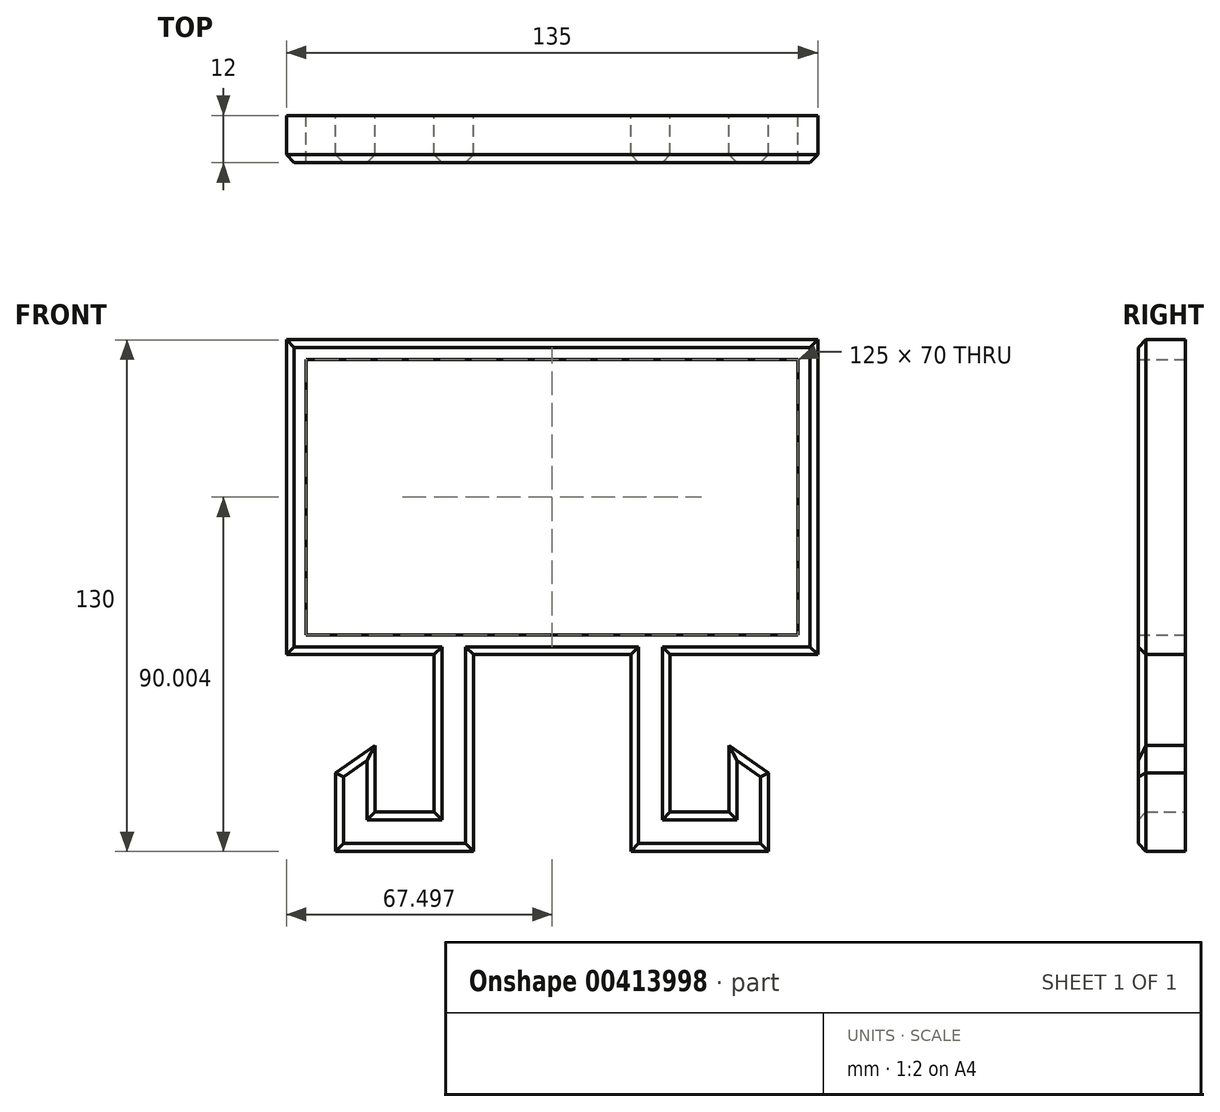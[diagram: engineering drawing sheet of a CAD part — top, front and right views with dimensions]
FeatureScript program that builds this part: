
annotation { "Feature Type Name" : "Feature", "Feature Type Description" : "" }
export const myFeature = defineFeature(function(context is Context, id is Id, definition is map)
    precondition{}
    {
        {
            var Q0;
            Q0=qCreatedBy(makeId("Front.planeOp"),FACE);
            var sketch = newSketch(context, id + "F0", { "sketchPlane" : qUnion([Q0])});
            skLineSegment(sketch, "E0.bottom", {"start": v(-108.38, 64.35) * mm, "end": v(16.62, 64.35) * mm});
            skLineSegment(sketch, "E0.top", {"start": v(-108.38, -5.65) * mm, "end": v(16.62, -5.65) * mm});
            skLineSegment(sketch, "E0.left", {"start": v(-108.38, 64.35) * mm, "end": v(-108.38, -5.65) * mm});
            skLineSegment(sketch, "E0.right", {"start": v(16.62, 64.35) * mm, "end": v(16.62, -5.65) * mm});
            skLineSegment(sketch, "E1.0", {"start": v(-113.38, 69.35) * mm, "end": v(21.62, 69.35) * mm});
            skLineSegment(sketch, "E1.1", {"start": v(-113.38, 69.35) * mm, "end": v(-113.38, -10.65) * mm});
            skLineSegment(sketch, "E1.2", {"start": v(-113.38, -10.65) * mm, "end": v(21.62, -10.65) * mm});
            skLineSegment(sketch, "E1.3", {"start": v(21.62, 69.35) * mm, "end": v(21.62, -10.65) * mm});
            skPoint(sketch, "E2", {"position": v(-73.94, -5.65) * mm});
            skPoint(sketch, "E3", {"position": v(-45.88, -10.65) * mm});
            skLineSegment(sketch, "E4", {"start": v(-45.88, -10.65) * mm, "end": v(-45.88, 23.81) * mm, "construction": true});
            skPoint(sketch, "E5", {"position": v(-65.88, -10.65) * mm});
            skLineSegment(sketch, "E6", {"start": v(-65.88, -10.65) * mm, "end": v(-65.88, -60.65) * mm});
            skLineSegment(sketch, "E7", {"start": v(-65.88, -60.65) * mm, "end": v(-100.88, -60.65) * mm});
            skLineSegment(sketch, "E8", {"start": v(-75.88, -50.65) * mm, "end": v(-75.88, -10.65) * mm});
            skLineSegment(sketch, "E9", {"start": v(-90.88, -40.65) * mm, "end": v(-90.88, -50.65) * mm});
            skLineSegment(sketch, "E10", {"start": v(-90.88, -50.65) * mm, "end": v(-75.88, -50.65) * mm});
            skLineSegment(sketch, "E11", {"start": v(-100.88, -40.65) * mm, "end": v(-90.88, -40.65) * mm});
            skLineSegment(sketch, "E12", {"start": v(-100.88, -40.65) * mm, "end": v(-100.88, -60.65) * mm});
            skLineSegment(sketch, "E13", {"start": v(-90.88, -40.65) * mm, "end": v(-90.88, -33.65) * mm});
            skLineSegment(sketch, "E14", {"start": v(-90.88, -33.65) * mm, "end": v(-100.88, -40.65) * mm});
            skLineSegment(sketch, "E15.MirrorCS", {"start": v(-0.88, -40.65) * mm, "end": v(-0.88, -33.65) * mm});
            skPoint(sketch, "E16.MirrorP", {"position": v(-25.88, -10.65) * mm});
            skLineSegment(sketch, "E17.MirrorCS", {"start": v(-0.88, -40.65) * mm, "end": v(-0.88, -50.65) * mm});
            skLineSegment(sketch, "E18.MirrorCS", {"start": v(9.12, -40.65) * mm, "end": v(-0.88, -40.65) * mm});
            skLineSegment(sketch, "E19.MirrorCS", {"start": v(-25.88, -60.65) * mm, "end": v(9.12, -60.65) * mm});
            skLineSegment(sketch, "E20.MirrorCS", {"start": v(9.12, -40.65) * mm, "end": v(9.12, -60.65) * mm});
            skLineSegment(sketch, "E21.MirrorCS", {"start": v(-0.88, -33.65) * mm, "end": v(9.12, -40.65) * mm});
            skLineSegment(sketch, "E22.MirrorCS", {"start": v(-0.88, -50.65) * mm, "end": v(-15.88, -50.65) * mm});
            skLineSegment(sketch, "E23.MirrorCS", {"start": v(-25.88, -10.65) * mm, "end": v(-25.88, -60.65) * mm});
            skLineSegment(sketch, "E24.MirrorCS", {"start": v(-15.88, -50.65) * mm, "end": v(-15.88, -10.65) * mm});
            skSolve(sketch);
        }
        {
            var Q0;
            Q0=makeQuery(id+"F0.imprint","IMPRINT",FACE,{"disambiguationData":[TD([[makeQuery(id+"F0.imprint","IMPRINT",EDGE,{"derivedFrom":sQuery(id+"F0.wireOp",EDGE,"E0.bottom")}),1.0]])]});
            var Q1;
            {var subQ1=sQuery(id+"F0.wireOp",EDGE,"E6");Q1=makeQuery(id+"F0.imprint","IMPRINT",FACE,{"disambiguationData":[TD([[makeQuery(id+"F0.imprint","IMPRINT",EDGE,{"derivedFrom":subQ1}),-1.0]])]});}
            var Q2;
            Q2=makeQuery(id+"F0.imprint","IMPRINT",FACE,{"disambiguationData":[TD([[makeQuery(id+"F0.imprint","IMPRINT",EDGE,{"derivedFrom":sQuery(id+"F0.wireOp",EDGE,"E17.MirrorCS")}),1.0]])]});
            var Q3;
            Q3=makeQuery(id+"F0.imprint","IMPRINT",FACE,{"disambiguationData":[TD([[makeQuery(id+"F0.imprint","IMPRINT",EDGE,{"derivedFrom":sQuery(id+"F0.wireOp",EDGE,"E11")}),1.0]])]});
            var Q4;
            Q4=makeQuery(id+"F0.imprint","IMPRINT",FACE,{"disambiguationData":[TD([[makeQuery(id+"F0.imprint","IMPRINT",EDGE,{"derivedFrom":sQuery(id+"F0.wireOp",EDGE,"E15.MirrorCS")}),-1.0]])]});
            extrude(context, id + "F1", {"entities" : qUnion([Q0, Q1, Q2, Q3, Q4]), "depth" : 12 * mm});
        }
        {
            var Q0;
            Q0=makeQuery(id+"F1.opExtrude","CAP_EDGE",EDGE,{"disambiguationData":[OSD([sQuery(id+"F0.wireOp",EDGE,"E1.3")])],"isStart":false});
            var Q1;
            Q1=makeQuery(id+"F1.opExtrude","CAP_EDGE",EDGE,{"disambiguationData":[OSD([sQuery(id+"F0.wireOp",EDGE,"E1.0")])],"isStart":false});
            var Q2;
            Q2=makeQuery(id+"F1.opExtrude","CAP_EDGE",EDGE,{"disambiguationData":[OSD([sQuery(id+"F0.wireOp",EDGE,"E1.1")])],"isStart":false});
            var Q3;
            {var subQ0=sQuery(id+"F0.wireOp",EDGE,"E1.2");Q3=makeQuery(id+"F1.opExtrude","CAP_EDGE",EDGE,{"disambiguationData":[OSD([subQ0]),TDD([makeQuery(id+"F0.imprint","IMPRINT",EDGE,{"disambiguationData":[TD([[makeQuery(id+"F0.imprint","INTERSECT",VERTEX,{"derivedFrom":[sQuery(id+"F0.wireOp",EDGE,"E1.1"),subQ0]}),-1.0]])],"derivedFrom":subQ0})])],"isStart":false});}
            var Q4;
            Q4=makeQuery(id+"F1.opExtrude","CAP_EDGE",EDGE,{"disambiguationData":[OSD([sQuery(id+"F0.wireOp",EDGE,"E8")])],"isStart":false});
            var Q5;
            Q5=makeQuery(id+"F1.opExtrude","CAP_EDGE",EDGE,{"disambiguationData":[OSD([sQuery(id+"F0.wireOp",EDGE,"E10")])],"isStart":false});
            var Q6;
            Q6=makeQuery(id+"F1.opExtrude","CAP_EDGE",EDGE,{"disambiguationData":[OSD([sQuery(id+"F0.wireOp",EDGE,"E9"),sQuery(id+"F0.wireOp",EDGE,"E13")])],"isStart":false});
            var Q7;
            Q7=makeQuery(id+"F1.opExtrude","CAP_EDGE",EDGE,{"disambiguationData":[OSD([sQuery(id+"F0.wireOp",EDGE,"E14")])],"isStart":false});
            var Q8;
            Q8=makeQuery(id+"F1.opExtrude","CAP_EDGE",EDGE,{"disambiguationData":[OSD([sQuery(id+"F0.wireOp",EDGE,"E12")])],"isStart":false});
            var Q9;
            Q9=makeQuery(id+"F1.opExtrude","CAP_EDGE",EDGE,{"disambiguationData":[OSD([sQuery(id+"F0.wireOp",EDGE,"E7")])],"isStart":false});
            var Q10;
            Q10=makeQuery(id+"F1.opExtrude","CAP_EDGE",EDGE,{"disambiguationData":[OSD([sQuery(id+"F0.wireOp",EDGE,"E6")])],"isStart":false});
            var Q11;
            {var subQ0=sQuery(id+"F0.wireOp",EDGE,"E1.2");Q11=makeQuery(id+"F1.opExtrude","CAP_EDGE",EDGE,{"disambiguationData":[OSD([subQ0]),TDD([makeQuery(id+"F0.imprint","IMPRINT",EDGE,{"disambiguationData":[TD([[makeQuery(id+"F0.imprint","INTERSECT",VERTEX,{"derivedFrom":[subQ0,sQuery(id+"F0.wireOp",EDGE,"E6")]}),-1.0]])],"derivedFrom":subQ0})])],"isStart":false});}
            var Q12;
            Q12=makeQuery(id+"F1.opExtrude","CAP_EDGE",EDGE,{"disambiguationData":[OSD([sQuery(id+"F0.wireOp",EDGE,"E23.MirrorCS")])],"isStart":false});
            var Q13;
            Q13=makeQuery(id+"F1.opExtrude","CAP_EDGE",EDGE,{"disambiguationData":[OSD([sQuery(id+"F0.wireOp",EDGE,"E19.MirrorCS")])],"isStart":false});
            var Q14;
            Q14=makeQuery(id+"F1.opExtrude","CAP_EDGE",EDGE,{"disambiguationData":[OSD([sQuery(id+"F0.wireOp",EDGE,"E20.MirrorCS")])],"isStart":false});
            var Q15;
            Q15=makeQuery(id+"F1.opExtrude","CAP_EDGE",EDGE,{"disambiguationData":[OSD([sQuery(id+"F0.wireOp",EDGE,"E21.MirrorCS")])],"isStart":false});
            var Q16;
            Q16=makeQuery(id+"F1.opExtrude","CAP_EDGE",EDGE,{"disambiguationData":[OSD([sQuery(id+"F0.wireOp",EDGE,"E15.MirrorCS"),sQuery(id+"F0.wireOp",EDGE,"E17.MirrorCS")])],"isStart":false});
            var Q17;
            Q17=makeQuery(id+"F1.opExtrude","CAP_EDGE",EDGE,{"disambiguationData":[OSD([sQuery(id+"F0.wireOp",EDGE,"E22.MirrorCS")])],"isStart":false});
            var Q18;
            Q18=makeQuery(id+"F1.opExtrude","CAP_EDGE",EDGE,{"disambiguationData":[OSD([sQuery(id+"F0.wireOp",EDGE,"E24.MirrorCS")])],"isStart":false});
            var Q19;
            {var subQ0=sQuery(id+"F0.wireOp",EDGE,"E1.2");Q19=makeQuery(id+"F1.opExtrude","CAP_EDGE",EDGE,{"disambiguationData":[OSD([subQ0]),TDD([makeQuery(id+"F0.imprint","IMPRINT",EDGE,{"disambiguationData":[TD([[makeQuery(id+"F0.imprint","INTERSECT",VERTEX,{"derivedFrom":[subQ0,sQuery(id+"F0.wireOp",EDGE,"E1.3")]}),1.0]])],"derivedFrom":subQ0})])],"isStart":false});}
            chamfer(context, id + "F2", {"entities" : qUnion([Q0, Q1, Q2, Q3, Q4, Q5, Q6, Q7, Q8, Q9, Q10, Q11, Q12, Q13, Q14, Q15, Q16, Q17, Q18, Q19]), "width" : 2 * mm, "tangentPropagation" : true});
        }
    });
